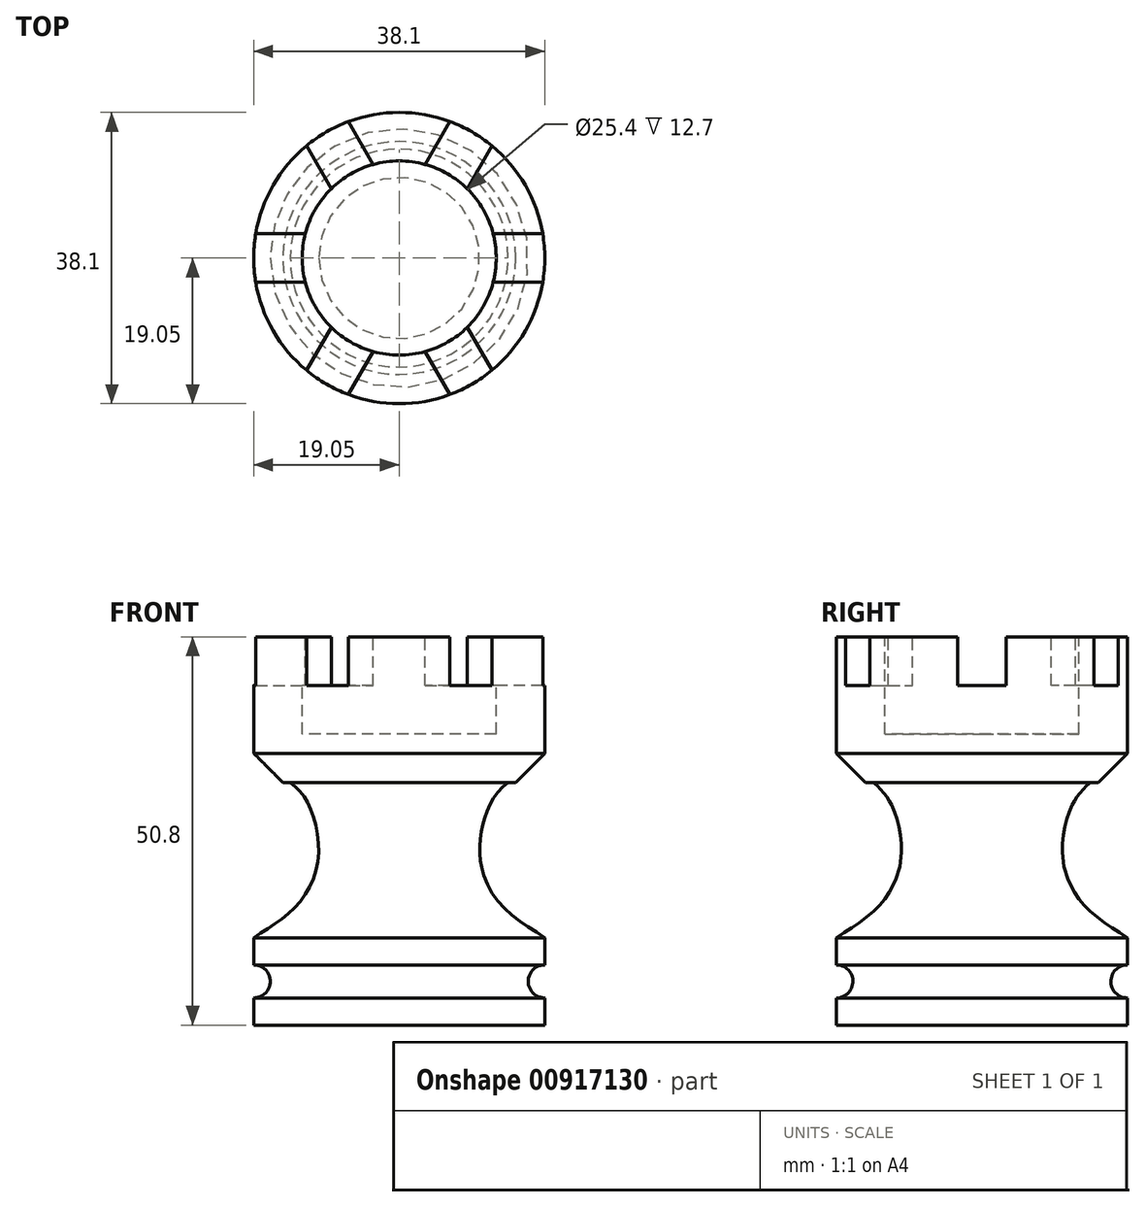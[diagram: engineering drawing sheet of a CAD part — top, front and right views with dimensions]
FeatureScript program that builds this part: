
annotation { "Feature Type Name" : "Feature", "Feature Type Description" : "" }
export const myFeature = defineFeature(function(context is Context, id is Id, definition is map)
    precondition{}
    {
        {
            var Q0;
            Q0=qCreatedBy(makeId("Front.planeOp"),FACE);
            var sketch = newSketch(context, id + "F0", { "sketchPlane" : qUnion([Q0])});
            skLineSegment(sketch, "E0", {"start": v(0, 0) * mm, "end": v(0, 50.8) * mm});
            skLineSegment(sketch, "E1", {"start": v(0, 0) * mm, "end": v(19.05, 0) * mm});
            skLineSegment(sketch, "E2", {"start": v(19.05, 0) * mm, "end": v(19.05, 11.43) * mm});
            skLineSegment(sketch, "E3", {"start": v(0, 31.75) * mm, "end": v(45.34, 31.75) * mm, "construction": true});
            skLineSegment(sketch, "E4.bottom", {"start": v(0, 31.75) * mm, "end": v(19.05, 31.75) * mm});
            skLineSegment(sketch, "E4.top", {"start": v(0, 34.92) * mm, "end": v(19.05, 34.92) * mm});
            skLineSegment(sketch, "E4.left", {"start": v(0, 31.75) * mm, "end": v(0, 34.92) * mm});
            skLineSegment(sketch, "E4.right", {"start": v(19.05, 31.75) * mm, "end": v(19.05, 34.92) * mm});
            skFitSpline(sketch, "E5", {"points": [v(19.05, 11.43) * mm, v(13.73, 15.32) * mm, v(10.64, 21.45) * mm, v(11.68, 28.43) * mm, v(14.25, 31.75) * mm], "startDerivative": vector(-20.72, 13.95) * mm, "endDerivative": vector(16.66, 12.87) * mm});
            skLineSegment(sketch, "E6.top", {"start": v(0, 50.8) * mm, "end": v(19.05, 50.8) * mm});
            skLineSegment(sketch, "E6.left", {"start": v(0, 34.92) * mm, "end": v(0, 50.8) * mm});
            skLineSegment(sketch, "E6.right", {"start": v(19.05, 34.92) * mm, "end": v(19.05, 50.8) * mm});
            skSolve(sketch);
        }
        {
            var Q0;
            {var subQ0=sQuery(id+"F0.wireOp",EDGE,"E4.top");Q0=makeQuery(id+"F0.imprint","IMPRINT",FACE,{"disambiguationData":[TD([[makeQuery(id+"F0.imprint","IMPRINT",EDGE,{"derivedFrom":subQ0}),1.0]])]});}
            var Q1;
            {var subQ5=sQuery(id+"F0.wireOp",EDGE,"E4.top");Q1=makeQuery(id+"F0.imprint","IMPRINT",FACE,{"disambiguationData":[TD([[makeQuery(id+"F0.imprint","IMPRINT",EDGE,{"derivedFrom":subQ5}),-1.0]])]});}
            var Q2;
            {var subQ0=sQuery(id+"F0.wireOp",EDGE,"E1");Q2=makeQuery(id+"F0.imprint","IMPRINT",FACE,{"disambiguationData":[TD([[makeQuery(id+"F0.imprint","IMPRINT",EDGE,{"derivedFrom":subQ0}),1.0]])]});}
            var Q3;
            Q3=sQuery(id+"F0.wireOp",EDGE,"E6.left");
            revolve(context, id + "F1", {"surfaceOperationType" : NewSurfaceOperationType.NEW, "entities" : qUnion([Q0, Q1, Q2]), "axis" : qUnion([Q3]), "revolveType" : RevolveType.FULL});
        }
        {
            var Q0;
            Q0=makeQuery(id+"F1.opRevolve","SWEPT_FACE",FACE,{"disambiguationData":[OSD([sQuery(id+"F0.wireOp",EDGE,"E6.top")])]});
            var sketch = newSketch(context, id + "F2", { "sketchPlane" : qUnion([Q0])});
            skCircle(sketch, "E7", {"center": v(0, 0) * mm, "radius": 12.7 * mm});
            skSolve(sketch);
        }
        {
            var Q0;
            Q0=makeQuery(id+"F2.imprint","IMPRINT",FACE,{"disambiguationData":[TD([[makeQuery(id+"F2.imprint","IMPRINT",EDGE,{"derivedFrom":sQuery(id+"F2.wireOp",EDGE,"E7")}),1.0]])]});
            extrude(context, id + "F3", {"entities" : qUnion([Q0]), "operationType" : NewBodyOperationType.REMOVE, "oppositeDirection" : true, "depth" : 12.7 * mm, "offsetDistance" : 25.4 * mm});
        }
        {
            var Q0;
            Q0=makeQuery(id+"F1.opRevolve","SWEPT_FACE",FACE,{"disambiguationData":[OSD([sQuery(id+"F0.wireOp",EDGE,"E6.top")])]});
            var sketch = newSketch(context, id + "F4", { "sketchPlane" : qUnion([Q0])});
            skLineSegment(sketch, "E8", {"start": v(0, 0) * mm, "end": v(25.6, 0) * mm, "construction": true});
            skLineSegment(sketch, "E9.bottom", {"start": v(25.6, -3.18) * mm, "end": v(7.16, -3.18) * mm});
            skLineSegment(sketch, "E9.top", {"start": v(25.6, 3.17) * mm, "end": v(7.16, 3.17) * mm});
            skLineSegment(sketch, "E9.left", {"start": v(25.6, -3.18) * mm, "end": v(25.6, 3.17) * mm});
            skLineSegment(sketch, "E9.right", {"start": v(7.16, -3.18) * mm, "end": v(7.16, 3.17) * mm});
            skPoint(sketch, "E9.middle", {"position": v(16.38, 0) * mm});
            skLineSegment(sketch, "E10.1.0", {"start": v(15.55, 20.59) * mm, "end": v(10.05, 23.76) * mm});
            skLineSegment(sketch, "E10.1.1", {"start": v(10.05, 23.76) * mm, "end": v(0.83, 7.79) * mm});
            skLineSegment(sketch, "E10.1.2", {"start": v(6.33, 4.61) * mm, "end": v(0.83, 7.79) * mm});
            skLineSegment(sketch, "E10.1.3", {"start": v(15.55, 20.59) * mm, "end": v(6.33, 4.61) * mm});
            skPoint(sketch, "E10.1.4", {"position": v(8.2, 14.19) * mm});
            skLineSegment(sketch, "E10.2.0", {"start": v(-10.05, 23.76) * mm, "end": v(-15.55, 20.59) * mm});
            skLineSegment(sketch, "E10.2.1", {"start": v(-15.55, 20.59) * mm, "end": v(-6.33, 4.61) * mm});
            skLineSegment(sketch, "E10.2.2", {"start": v(-0.83, 7.79) * mm, "end": v(-6.33, 4.61) * mm});
            skLineSegment(sketch, "E10.2.3", {"start": v(-10.05, 23.76) * mm, "end": v(-0.83, 7.79) * mm});
            skPoint(sketch, "E10.2.4", {"position": v(-8.2, 14.19) * mm});
            skLineSegment(sketch, "E10.3.0", {"start": v(-25.6, 3.18) * mm, "end": v(-25.6, -3.17) * mm});
            skLineSegment(sketch, "E10.3.1", {"start": v(-25.6, -3.17) * mm, "end": v(-7.16, -3.17) * mm});
            skLineSegment(sketch, "E10.3.2", {"start": v(-7.16, 3.18) * mm, "end": v(-7.16, -3.17) * mm});
            skLineSegment(sketch, "E10.3.3", {"start": v(-25.6, 3.18) * mm, "end": v(-7.16, 3.18) * mm});
            skPoint(sketch, "E10.3.4", {"position": v(-16.38, 0) * mm});
            skLineSegment(sketch, "E10.4.0", {"start": v(-15.55, -20.59) * mm, "end": v(-10.05, -23.76) * mm});
            skLineSegment(sketch, "E10.4.1", {"start": v(-10.05, -23.76) * mm, "end": v(-0.83, -7.79) * mm});
            skLineSegment(sketch, "E10.4.2", {"start": v(-6.33, -4.61) * mm, "end": v(-0.83, -7.79) * mm});
            skLineSegment(sketch, "E10.4.3", {"start": v(-15.55, -20.59) * mm, "end": v(-6.33, -4.61) * mm});
            skPoint(sketch, "E10.4.4", {"position": v(-8.2, -14.19) * mm});
            skLineSegment(sketch, "E10.5.0", {"start": v(10.05, -23.76) * mm, "end": v(15.55, -20.59) * mm});
            skLineSegment(sketch, "E10.5.1", {"start": v(15.55, -20.59) * mm, "end": v(6.33, -4.61) * mm});
            skLineSegment(sketch, "E10.5.2", {"start": v(0.83, -7.79) * mm, "end": v(6.33, -4.61) * mm});
            skLineSegment(sketch, "E10.5.3", {"start": v(10.05, -23.76) * mm, "end": v(0.83, -7.79) * mm});
            skPoint(sketch, "E10.5.4", {"position": v(8.2, -14.19) * mm});
            skPoint(sketch, "E10.center", {"position": v(0, 0) * mm});
            skSolve(sketch);
        }
        {
            var Q0;
            Q0 = qSketchRegion(id + "F4", true);
            extrude(context, id + "F5", {"entities" : qUnion([Q0]), "operationType" : NewBodyOperationType.REMOVE, "oppositeDirection" : true, "depth" : 6.35 * mm, "offsetDistance" : 25.4 * mm});
        }
        {
            var Q0;
            Q0=makeQuery(id+"F1.opRevolve","SWEPT_EDGE",EDGE,{"disambiguationData":[OSD([sQuery(id+"F0.wireOp",EDGE,"E4.bottom"),sQuery(id+"F0.wireOp",EDGE,"E4.right")])]});
            chamfer(context, id + "F6", {"entities" : qUnion([Q0]), "width" : 3.8 * mm, "tangentPropagation" : true});
        }
        {
            var Q0;
            Q0=qCreatedBy(makeId("Front.planeOp"),FACE);
            var sketch = newSketch(context, id + "F7", { "sketchPlane" : qUnion([Q0])});
            skLineSegment(sketch, "E11", {"start": v(0, 5.72) * mm, "end": v(19.05, 5.72) * mm, "construction": true});
            skCircle(sketch, "E12", {"center": v(19.05, 5.72) * mm, "radius": 2.16 * mm});
            skLineSegment(sketch, "E13", {"start": v(19.05, 11.43) * mm, "end": v(19.05, 0) * mm});
            skSolve(sketch);
        }
        {
            var Q0;
            Q0 = qSketchRegion(id + "F7", true);
            var Q1;
            Q1=makeQuery(id+"F1.opRevolve","SWEPT_FACE",FACE,{"disambiguationData":[OSD([sQuery(id+"F0.wireOp",EDGE,"E2")])]});
            revolve(context, id + "F8", {"operationType" : NewBodyOperationType.REMOVE, "surfaceOperationType" : NewSurfaceOperationType.NEW, "entities" : qUnion([Q0]), "axis" : qUnion([Q1]), "revolveType" : RevolveType.FULL, "oppositeDirection" : true});
        }
    });
